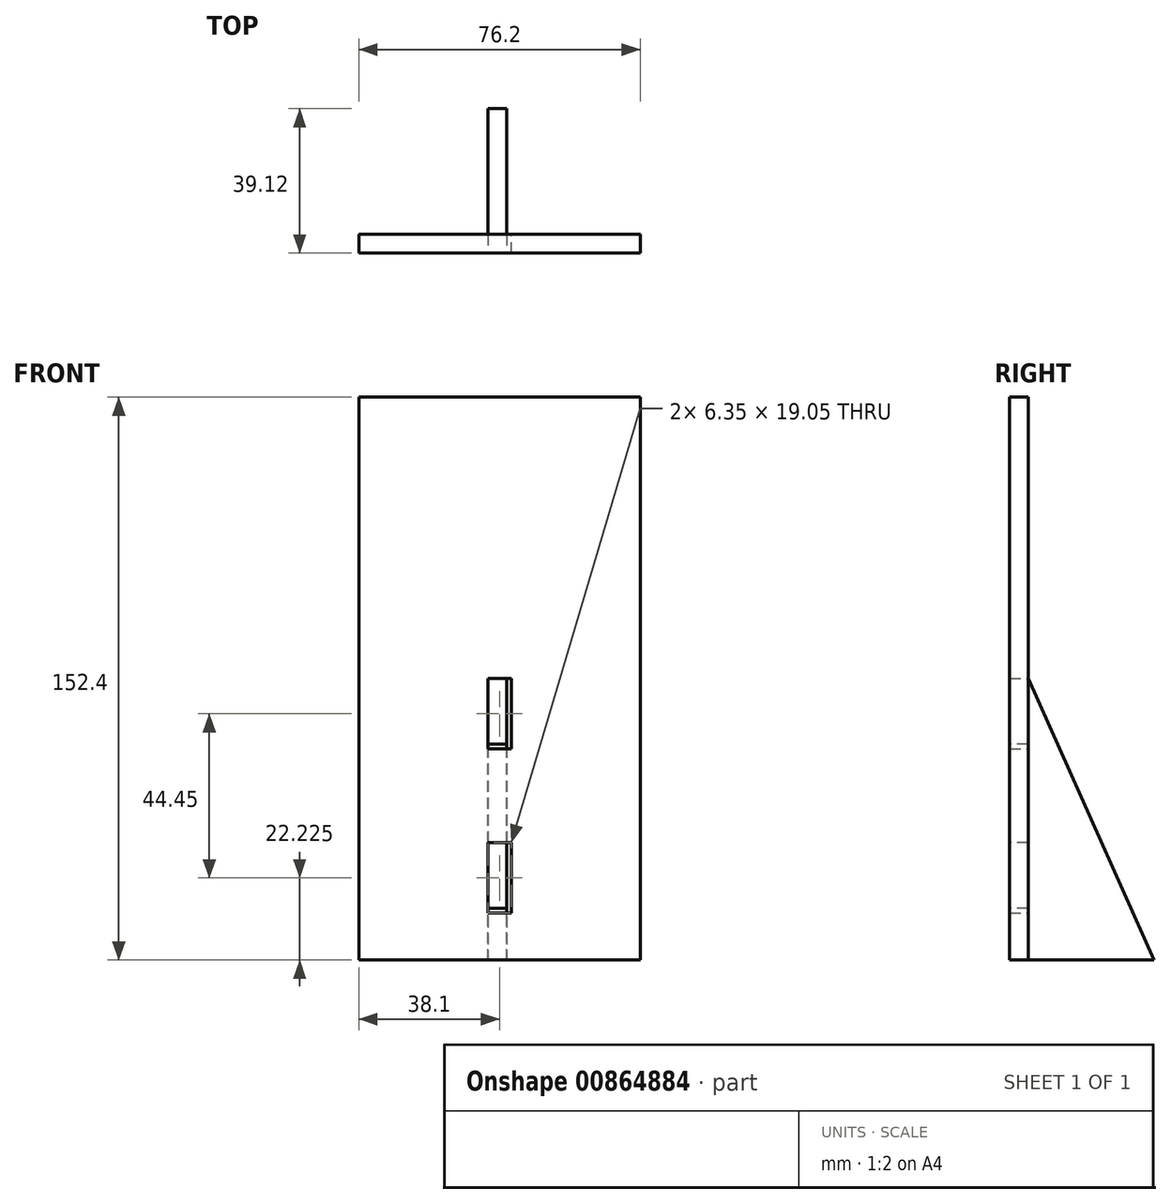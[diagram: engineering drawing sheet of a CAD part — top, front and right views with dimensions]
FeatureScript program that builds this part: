
annotation { "Feature Type Name" : "Feature", "Feature Type Description" : "" }
export const myFeature = defineFeature(function(context is Context, id is Id, definition is map)
    precondition{}
    {
        {
            var Q0;
            Q0=qCreatedBy(makeId("Front.planeOp"),FACE);
            var sketch = newSketch(context, id + "F0", { "sketchPlane" : qUnion([Q0])});
            skLineSegment(sketch, "E0.bottom", {"start": v(0, 0) * mm, "end": v(76.2, 0) * mm});
            skLineSegment(sketch, "E0.top", {"start": v(0, 152.4) * mm, "end": v(76.2, 152.4) * mm});
            skLineSegment(sketch, "E0.left", {"start": v(0, 0) * mm, "end": v(0, 152.4) * mm});
            skLineSegment(sketch, "E0.right", {"start": v(76.2, 0) * mm, "end": v(76.2, 152.4) * mm});
            skLineSegment(sketch, "E1.bottom", {"start": v(34.93, 76.2) * mm, "end": v(41.28, 76.2) * mm});
            skLineSegment(sketch, "E1.top", {"start": v(34.93, 57.15) * mm, "end": v(41.28, 57.15) * mm});
            skLineSegment(sketch, "E1.left", {"start": v(34.93, 76.2) * mm, "end": v(34.93, 57.15) * mm});
            skLineSegment(sketch, "E1.right", {"start": v(41.28, 76.2) * mm, "end": v(41.28, 57.15) * mm});
            skLineSegment(sketch, "E2.bottom", {"start": v(41.28, 31.75) * mm, "end": v(34.93, 31.75) * mm});
            skLineSegment(sketch, "E2.top", {"start": v(41.28, 12.7) * mm, "end": v(34.93, 12.7) * mm});
            skLineSegment(sketch, "E2.left", {"start": v(41.28, 31.75) * mm, "end": v(41.28, 12.7) * mm});
            skLineSegment(sketch, "E2.right", {"start": v(34.93, 31.75) * mm, "end": v(34.93, 12.7) * mm});
            skSolve(sketch);
        }
        {
            var Q0;
            Q0=makeQuery(id+"F0.imprint","IMPRINT",FACE,{"disambiguationData":[TD([[makeQuery(id+"F0.imprint","IMPRINT",EDGE,{"derivedFrom":sQuery(id+"F0.wireOp",EDGE,"E0.bottom")}),1.0]])]});
            extrude(context, id + "F1", {"entities" : qUnion([Q0]), "depth" : 5.08 * mm, "offsetDistance" : 25.4 * mm});
        }
        {
            var Q0;
            Q0=makeQuery(id+"F1.opExtrude","SWEPT_FACE",FACE,{"disambiguationData":[OSD([sQuery(id+"F0.wireOp",EDGE,"E1.left")])]});
            var sketch = newSketch(context, id + "F2", { "sketchPlane" : qUnion([Q0])});
            skPoint(sketch, "E3.0", {"position": v(0, 76.2) * mm});
            skPoint(sketch, "E4.0", {"position": v(0, 57.15) * mm});
            skPoint(sketch, "E5.0", {"position": v(0, 31.75) * mm});
            skPoint(sketch, "E6.0", {"position": v(0, 12.7) * mm});
            skLineSegment(sketch, "E7", {"start": v(0, 76.2) * mm, "end": v(34.04, 0) * mm});
            skLineSegment(sketch, "E8", {"start": v(34.04, 0) * mm, "end": v(0, 0) * mm});
            skLineSegment(sketch, "E9", {"start": v(0, 0) * mm, "end": v(0, 76.2) * mm});
            skLineSegment(sketch, "E10.bottom", {"start": v(0, 76.2) * mm, "end": v(-5.08, 76.2) * mm});
            skLineSegment(sketch, "E10.top", {"start": v(0, 58.42) * mm, "end": v(-5.08, 58.42) * mm});
            skLineSegment(sketch, "E10.left", {"start": v(0, 76.2) * mm, "end": v(0, 58.42) * mm});
            skLineSegment(sketch, "E10.right", {"start": v(-5.08, 76.2) * mm, "end": v(-5.08, 58.42) * mm});
            skLineSegment(sketch, "E11.bottom", {"start": v(0, 31.75) * mm, "end": v(-5.08, 31.75) * mm});
            skLineSegment(sketch, "E11.top", {"start": v(0, 13.97) * mm, "end": v(-5.08, 13.97) * mm});
            skLineSegment(sketch, "E11.left", {"start": v(0, 31.75) * mm, "end": v(0, 13.97) * mm});
            skLineSegment(sketch, "E11.right", {"start": v(-5.08, 31.75) * mm, "end": v(-5.08, 13.97) * mm});
            skSolve(sketch);
        }
        {
            var Q0;
            Q0=qSketchRegion(id+"F2",true);
            extrude(context, id + "F3", {"entities" : qUnion([Q0]), "depth" : 5.08 * mm, "offsetDistance" : 25.4 * mm});
        }
    });
